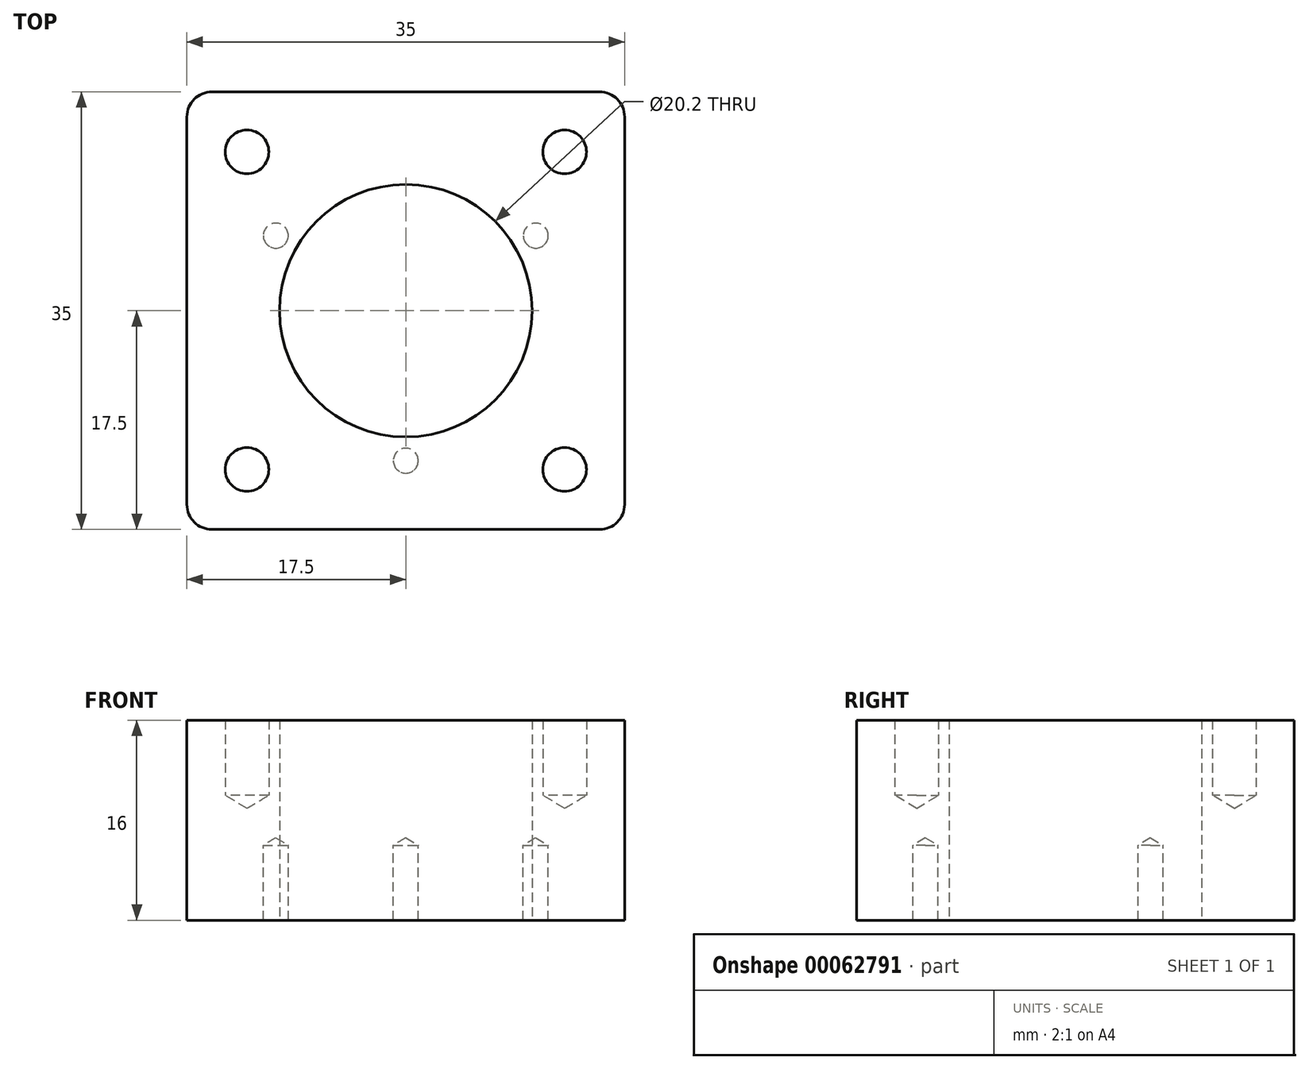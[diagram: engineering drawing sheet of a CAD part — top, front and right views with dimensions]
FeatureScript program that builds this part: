
annotation { "Feature Type Name" : "Feature", "Feature Type Description" : "" }
export const myFeature = defineFeature(function(context is Context, id is Id, definition is map)
    precondition{}
    {
        {
            var Q0;
            Q0=qCreatedBy(makeId("Top.planeOp"),FACE);
            var sketch = newSketch(context, id + "F0", { "sketchPlane" : qUnion([Q0])});
            skLineSegment(sketch, "E0.rect.bottom", {"start": v(15.5, -17.5) * mm, "end": v(-15.5, -17.5) * mm});
            skLineSegment(sketch, "E0.rect.top", {"start": v(15.5, 17.5) * mm, "end": v(-15.5, 17.5) * mm});
            skLineSegment(sketch, "E0.rect.left", {"start": v(17.5, -15.5) * mm, "end": v(17.5, 15.5) * mm});
            skLineSegment(sketch, "E0.rect.right", {"start": v(-17.5, -15.5) * mm, "end": v(-17.5, 15.5) * mm});
            skPoint(sketch, "E0.rect.middle", {"position": v(0, 0) * mm});
            skPoint(sketch, "E1.visualSharp", {"position": v(-17.5, 17.5) * mm});
            skArc(sketch, "E1.filletArc", {"start": v(-15.5, 17.5) * mm, "mid": v(-16.91, 16.91) * mm, "end": v(-17.5, 15.5) * mm});
            skPoint(sketch, "E2.visualSharp", {"position": v(-17.5, -17.5) * mm});
            skArc(sketch, "E2.filletArc", {"start": v(-17.5, -15.5) * mm, "mid": v(-16.91, -16.91) * mm, "end": v(-15.5, -17.5) * mm});
            skPoint(sketch, "E3.visualSharp", {"position": v(17.5, -17.5) * mm});
            skArc(sketch, "E3.filletArc", {"start": v(15.5, -17.5) * mm, "mid": v(16.91, -16.91) * mm, "end": v(17.5, -15.5) * mm});
            skPoint(sketch, "E4.visualSharp", {"position": v(17.5, 17.5) * mm});
            skArc(sketch, "E4.filletArc", {"start": v(17.5, 15.5) * mm, "mid": v(16.91, 16.91) * mm, "end": v(15.5, 17.5) * mm});
            skCircle(sketch, "E5", {"center": v(0, 0) * mm, "radius": 10.1 * mm});
            skSolve(sketch);
        }
        {
            var Q0;
            Q0=makeQuery(id+"F0.imprint","IMPRINT",FACE,{"disambiguationData":[TD([[makeQuery(id+"F0.imprint","IMPRINT",EDGE,{"derivedFrom":sQuery(id+"F0.wireOp",EDGE,"E0.rect.bottom")}),-1.0]])]});
            extrude(context, id + "F1", {"entities" : qUnion([Q0]), "depth" : 16 * mm});
        }
        {
            var Q0;
            Q0=makeQuery(id+"F1.opExtrude","CAP_FACE",FACE,{"disambiguationData":[OSD([sQuery(id+"F0.wireOp",EDGE,"E0.rect.bottom"),sQuery(id+"F0.wireOp",EDGE,"E0.rect.top"),sQuery(id+"F0.wireOp",EDGE,"E0.rect.left"),sQuery(id+"F0.wireOp",EDGE,"E0.rect.right"),sQuery(id+"F0.wireOp",EDGE,"E1.filletArc"),sQuery(id+"F0.wireOp",EDGE,"E2.filletArc"),sQuery(id+"F0.wireOp",EDGE,"E3.filletArc"),sQuery(id+"F0.wireOp",EDGE,"E4.filletArc"),sQuery(id+"F0.wireOp",EDGE,"E5")])],"isStart":false});
            var sketch = newSketch(context, id + "F2", { "sketchPlane" : qUnion([Q0])});
            skPoint(sketch, "E6", {"position": v(-12.7, 12.7) * mm});
            skPoint(sketch, "E7.MirrorP", {"position": v(12.7, 12.7) * mm});
            skPoint(sketch, "E8.MirrorP", {"position": v(12.7, -12.7) * mm});
            skPoint(sketch, "E9.MirrorP", {"position": v(-12.7, -12.7) * mm});
            skSolve(sketch);
        }
        {
            var Q0;
            Q0=sQuery(id+"F2.wireOp",VERTEX,"E6");
            var Q1;
            Q1=sQuery(id+"F2.wireOp",VERTEX,"E7.MirrorP");
            var Q2;
            Q2=sQuery(id+"F2.wireOp",VERTEX,"E8.MirrorP");
            var Q3;
            Q3=sQuery(id+"F2.wireOp",VERTEX,"E9.MirrorP");
            var Q4;
            Q4=makeQuery(id+"F1.opExtrude","SWEPT_BODY",BODY,{"disambiguationData":[OSD([sQuery(id+"F0.wireOp",EDGE,"E0.rect.bottom"),sQuery(id+"F0.wireOp",EDGE,"E0.rect.top"),sQuery(id+"F0.wireOp",EDGE,"E0.rect.left"),sQuery(id+"F0.wireOp",EDGE,"E0.rect.right"),sQuery(id+"F0.wireOp",EDGE,"E1.filletArc"),sQuery(id+"F0.wireOp",EDGE,"E2.filletArc"),sQuery(id+"F0.wireOp",EDGE,"E3.filletArc"),sQuery(id+"F0.wireOp",EDGE,"E4.filletArc"),sQuery(id+"F0.wireOp",EDGE,"E5")])]});
            hole(context, id + "F3", {"style" : HoleStyle.SIMPLE, "holeDiameter" : 3.5 * mm, "endStyle" : HoleEndStyle.BLIND, "holeDepth" : 6 * mm, "locations" : qUnion([Q0, Q1, Q2, Q3]), "scope" : qUnion([Q4])});
        }
        {
            var Q0;
            Q0=makeQuery(id+"F1.opExtrude","CAP_FACE",FACE,{"disambiguationData":[OSD([sQuery(id+"F0.wireOp",EDGE,"E0.rect.bottom"),sQuery(id+"F0.wireOp",EDGE,"E0.rect.top"),sQuery(id+"F0.wireOp",EDGE,"E0.rect.left"),sQuery(id+"F0.wireOp",EDGE,"E0.rect.right"),sQuery(id+"F0.wireOp",EDGE,"E1.filletArc"),sQuery(id+"F0.wireOp",EDGE,"E2.filletArc"),sQuery(id+"F0.wireOp",EDGE,"E3.filletArc"),sQuery(id+"F0.wireOp",EDGE,"E4.filletArc"),sQuery(id+"F0.wireOp",EDGE,"E5")])],"isStart":true});
            var sketch = newSketch(context, id + "F4", { "sketchPlane" : qUnion([Q0])});
            skPoint(sketch, "E10", {"position": v(0, 12) * mm});
            skPoint(sketch, "E11", {"position": v(0, 0) * mm});
            skPoint(sketch, "E12", {"position": v(-10.4, -6) * mm});
            skPoint(sketch, "E13", {"position": v(10.4, -6) * mm});
            skLineSegment(sketch, "E14", {"start": v(0, 12) * mm, "end": v(10.4, -6) * mm, "construction": true});
            skLineSegment(sketch, "E15", {"start": v(0, 12) * mm, "end": v(-10.4, -6) * mm, "construction": true});
            skLineSegment(sketch, "E16", {"start": v(10.4, -6) * mm, "end": v(-10.4, -6) * mm, "construction": true});
            skSolve(sketch);
        }
        {
            var Q0;
            Q0=sQuery(id+"F4.wireOp",VERTEX,"E10");
            var Q1;
            Q1=sQuery(id+"F4.wireOp",VERTEX,"E13");
            var Q2;
            Q2=sQuery(id+"F4.wireOp",VERTEX,"E12");
            var Q3;
            Q3=makeQuery(id+"F1.opExtrude","SWEPT_BODY",BODY,{"disambiguationData":[OSD([sQuery(id+"F0.wireOp",EDGE,"E0.rect.bottom"),sQuery(id+"F0.wireOp",EDGE,"E0.rect.top"),sQuery(id+"F0.wireOp",EDGE,"E0.rect.left"),sQuery(id+"F0.wireOp",EDGE,"E0.rect.right"),sQuery(id+"F0.wireOp",EDGE,"E1.filletArc"),sQuery(id+"F0.wireOp",EDGE,"E2.filletArc"),sQuery(id+"F0.wireOp",EDGE,"E3.filletArc"),sQuery(id+"F0.wireOp",EDGE,"E4.filletArc"),sQuery(id+"F0.wireOp",EDGE,"E5")])]});
            hole(context, id + "F5", {"style" : HoleStyle.SIMPLE, "holeDiameter" : 2 * mm, "endStyle" : HoleEndStyle.BLIND, "holeDepth" : 6 * mm, "locations" : qUnion([Q0, Q1, Q2]), "scope" : qUnion([Q3])});
        }
    });
